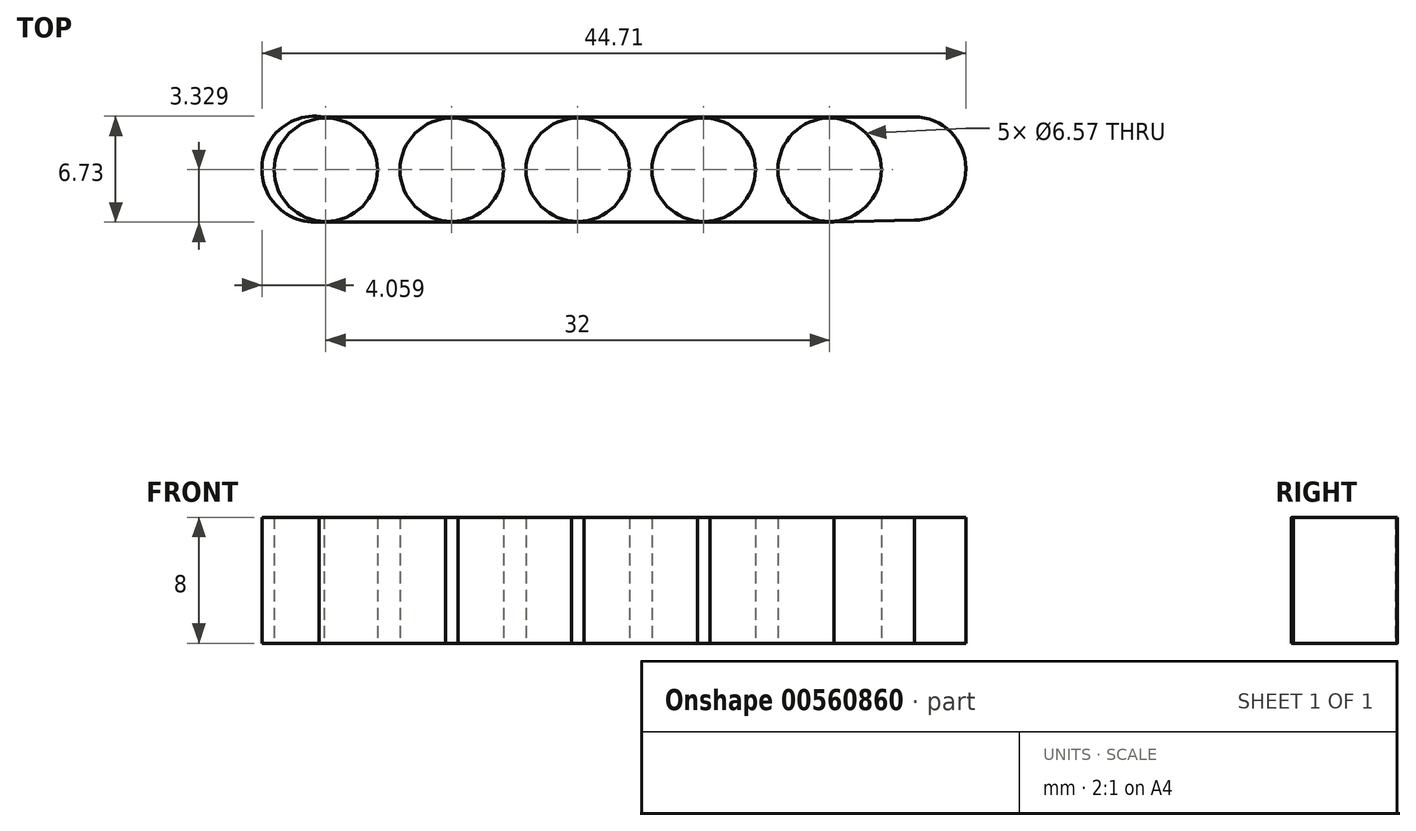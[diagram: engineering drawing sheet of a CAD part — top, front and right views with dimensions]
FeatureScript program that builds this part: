
annotation { "Feature Type Name" : "Feature", "Feature Type Description" : "" }
export const myFeature = defineFeature(function(context is Context, id is Id, definition is map)
    precondition{}
    {
        {
            var Q0;
            Q0=qCreatedBy(makeId("Top.planeOp"),FACE);
            var sketch = newSketch(context, id + "F0", { "sketchPlane" : qUnion([Q0])});
            skArc(sketch, "E0", {"start": v(-18.03, 4.17) * mm, "mid": v(-21.97, 1.02) * mm, "end": v(-18.35, -2.5) * mm});
            skLineSegment(sketch, "E1", {"start": v(-18.03, 4.17) * mm, "end": v(14.32, 4.17) * mm});
            skLineSegment(sketch, "E2", {"start": v(-18.35, -2.5) * mm, "end": v(14.35, -2.5) * mm});
            skCircle(sketch, "E3.2.0.1", {"center": v(14.09, 0.82) * mm, "radius": 3.29 * mm});
            skCircle(sketch, "E4.1.0.0", {"center": v(6.09, 0.82) * mm, "radius": 3.29 * mm});
            skCircle(sketch, "E4.1.0.1", {"center": v(6.09, 0.82) * mm, "radius": 3.33 * mm});
            skCircle(sketch, "E4.2.0.0", {"center": v(-1.91, 0.82) * mm, "radius": 3.29 * mm});
            skCircle(sketch, "E4.2.0.1", {"center": v(-1.91, 0.82) * mm, "radius": 3.33 * mm});
            skCircle(sketch, "E4.3.0.0", {"center": v(-9.91, 0.82) * mm, "radius": 3.29 * mm});
            skCircle(sketch, "E4.3.0.1", {"center": v(-9.91, 0.82) * mm, "radius": 3.33 * mm});
            skCircle(sketch, "E4.4.0.0", {"center": v(-17.91, 0.82) * mm, "radius": 3.29 * mm});
            skLineSegment(sketch, "E4.direction1", {"start": v(14.09, 0.82) * mm, "end": v(6.09, 0.82) * mm, "construction": true});
            skPoint(sketch, "E5.centerSnap0", {"position": v(10.09, 0.82) * mm});
            skLineSegment(sketch, "E6", {"start": v(14.32, 4.17) * mm, "end": v(19.47, 4.17) * mm});
            skLineSegment(sketch, "E7", {"start": v(19.47, -2.38) * mm, "end": v(14.35, -2.5) * mm});
            skArc(sketch, "E8", {"start": v(19.47, -2.38) * mm, "mid": v(22.74, 0.9) * mm, "end": v(19.47, 4.17) * mm});
            skSolve(sketch);
        }
        {
            var Q0;
            Q0=qSketchRegion(id+"F0",true);
            extrude(context, id + "F1", {"entities" : qUnion([Q0]), "depth" : 8 * mm, "offsetDistance" : 25.4 * mm});
        }
    });
